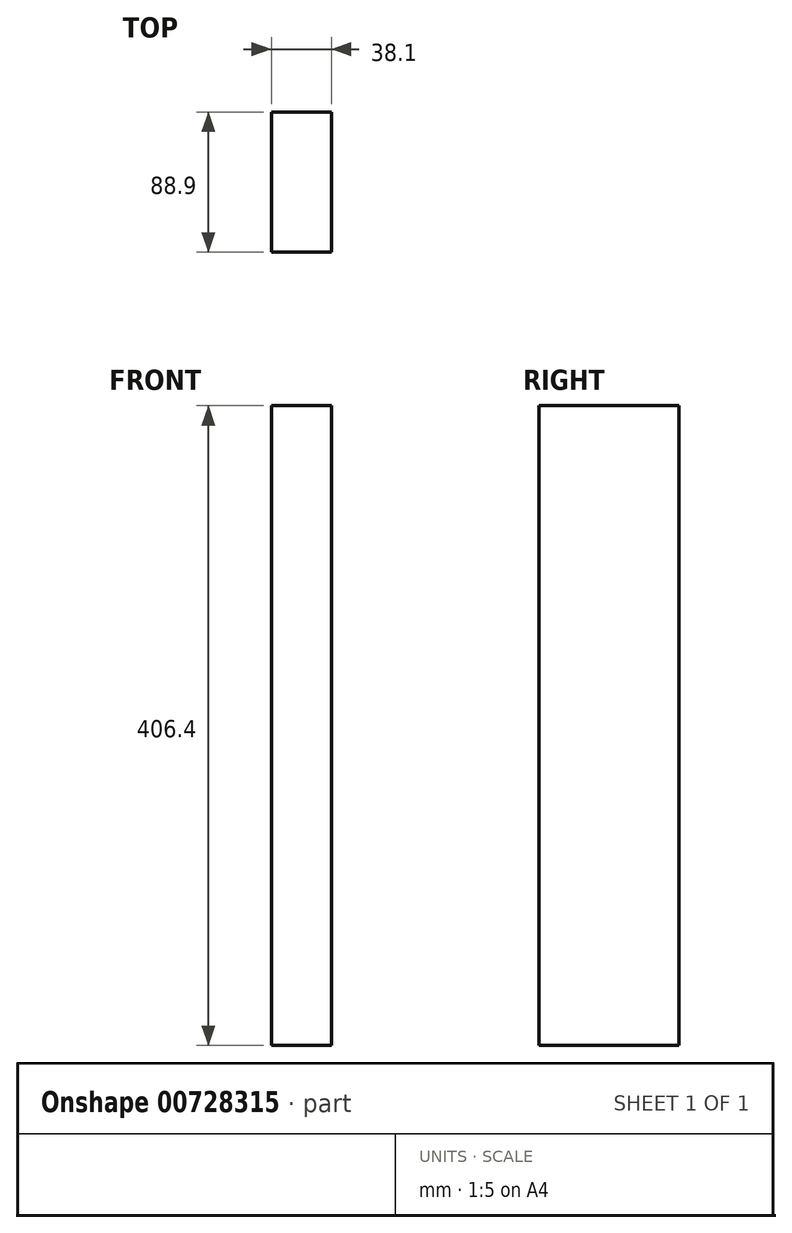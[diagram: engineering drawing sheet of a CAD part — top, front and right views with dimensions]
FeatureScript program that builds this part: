
annotation { "Feature Type Name" : "Feature", "Feature Type Description" : "" }
export const myFeature = defineFeature(function(context is Context, id is Id, definition is map)
    precondition{}
    {
        {
            var Q0;
            Q0=qCreatedBy(makeId("Front.planeOp"),FACE);
            var sketch = newSketch(context, id + "F0", { "sketchPlane" : qUnion([Q0])});
            skLineSegment(sketch, "E0.bottom", {"start": v(-19.05, -203.2) * mm, "end": v(19.05, -203.2) * mm});
            skLineSegment(sketch, "E0.top", {"start": v(-19.05, 203.2) * mm, "end": v(19.05, 203.2) * mm});
            skLineSegment(sketch, "E0.left", {"start": v(-19.05, -203.2) * mm, "end": v(-19.05, 203.2) * mm});
            skLineSegment(sketch, "E0.right", {"start": v(19.05, -203.2) * mm, "end": v(19.05, 203.2) * mm});
            skPoint(sketch, "E0.middle", {"position": v(0, 0) * mm});
            skSolve(sketch);
        }
        {
            var Q0;
            Q0=qSketchRegion(id+"F0",true);
            extrude(context, id + "F1", {"entities" : qUnion([Q0]), "depth" : 88.9 * mm});
        }
    });
